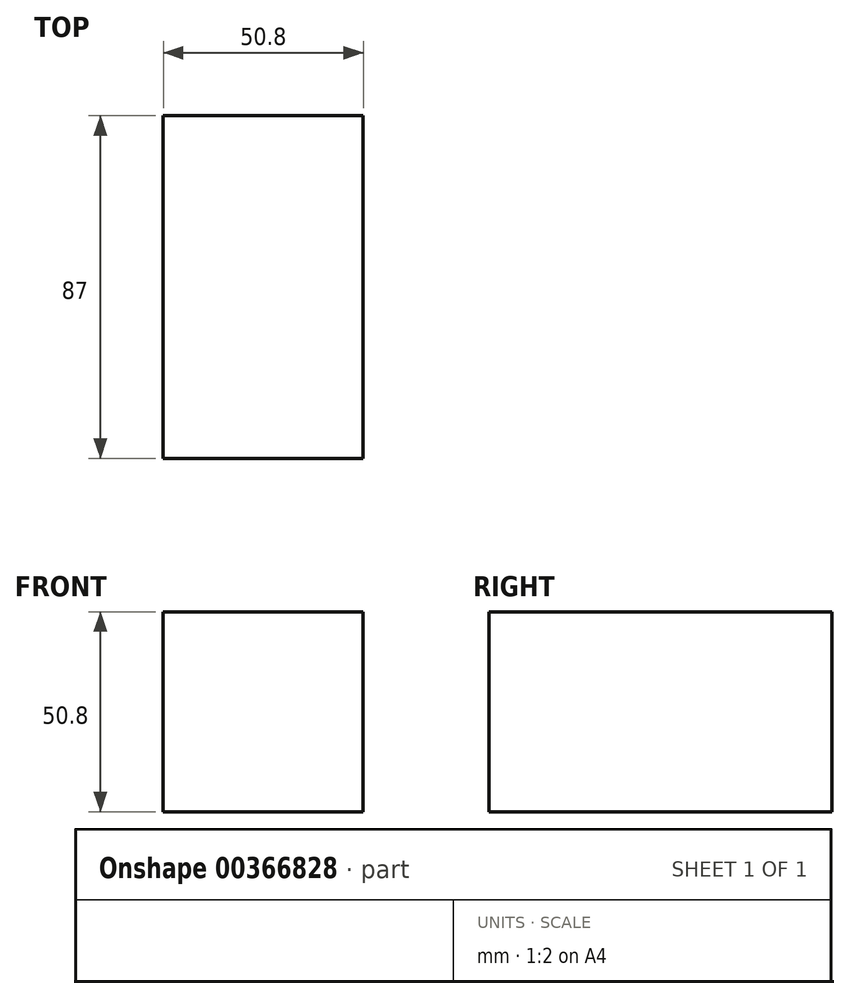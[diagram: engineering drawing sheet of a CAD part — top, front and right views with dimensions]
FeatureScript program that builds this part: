
annotation { "Feature Type Name" : "Feature", "Feature Type Description" : "" }
export const myFeature = defineFeature(function(context is Context, id is Id, definition is map)
    precondition{}
    {
        {
            var Q0;
            Q0=qCreatedBy(makeId("Front.planeOp"),FACE);
            var sketch = newSketch(context, id + "F0", { "sketchPlane" : qUnion([Q0])});
            skLineSegment(sketch, "E0.bottom", {"start": v(-32.9, 17.76) * mm, "end": v(-83.7, 17.76) * mm});
            skLineSegment(sketch, "E0.top", {"start": v(-32.9, 68.56) * mm, "end": v(-83.7, 68.56) * mm});
            skLineSegment(sketch, "E0.left", {"start": v(-32.9, 17.76) * mm, "end": v(-32.9, 68.56) * mm});
            skLineSegment(sketch, "E0.right", {"start": v(-83.7, 17.76) * mm, "end": v(-83.7, 68.56) * mm});
            skPoint(sketch, "E0.middle", {"position": v(-58.3, 43.16) * mm});
            skSolve(sketch);
        }
        {
            var Q0;
            Q0=makeQuery(id+"F0.imprint","IMPRINT",FACE,{"disambiguationData":[TD([[makeQuery(id+"F0.imprint","IMPRINT",EDGE,{"derivedFrom":sQuery(id+"F0.wireOp",EDGE,"E0.bottom")}),-1.0]])]});
            extrude(context, id + "F1", {"entities" : qUnion([Q0]), "depth" : 87 * mm});
        }
    });
